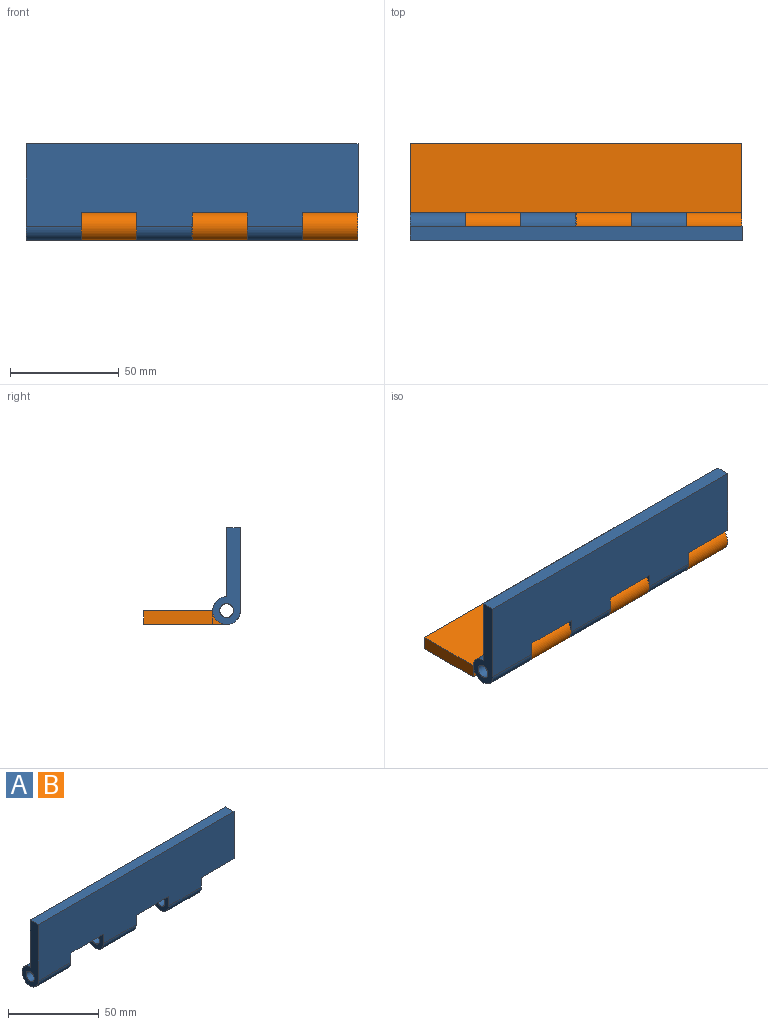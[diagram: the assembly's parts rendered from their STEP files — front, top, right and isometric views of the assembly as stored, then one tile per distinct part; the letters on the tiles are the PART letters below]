
ASSEMBLY  parts=2 mates=1
PART A: 19 faces, bbox 152.4x12.7x44.5 mm
  f0: cylinder r=6.35mm len=25.4mm, axis (-1,0,0), area 760.1mm2, adj f3,f4,f14,f18
  f1: cylinder r=6.35mm len=25.4mm, axis (-1,0,0), area 760.1mm2, adj f3,f4,f10,f15
  f2: cylinder r=6.35mm len=25.4mm, axis (-1,0,0), area 760.1mm2, adj f3,f4,f7,f11
  f3: plane 152.4x38.1mm, normal (0,-1,0), area 5322.6mm2, adj f0,f1,f2,f5,f6,f7,f9,f10
  f4: plane 152.4x31.75mm, normal (0,1,0), area 4838.7mm2, adj f0,f1,f2,f5,f6,f7,f9,f13
  f5: plane 152.4x6.35mm, normal (0,0,1), area 967.7mm2, adj f3,f4,f6,f7
  f6: plane 31.75x6.35mm, normal (1,0,0), area 201.6mm2, adj f3,f4,f5,f17
  f7: plane 44.45x12.7mm, normal (-1,0,0), area 305.3mm2, adj f2,f3,f4,f5,f8
  f8: cylinder r=3.17mm len=25.4mm, axis (1,0,0), area 506.7mm2, adj f7,f11
  f9: plane 25.4x6.35mm, normal (0,0,-1), area 161.3mm2, adj f3,f4,f10,f11
  f10: plane 12.7x12.7mm, normal (-1,0,0), area 103.7mm2, adj f1,f3,f9,f12
  f11: plane 12.7x12.7mm, normal (1,0,0), area 103.7mm2, adj f2,f3,f8,f9
  f12: cylinder r=3.17mm len=25.4mm, axis (1,0,0), area 506.7mm2, adj f10,f15
  f13: plane 25.4x6.35mm, normal (0,0,-1), area 161.3mm2, adj f3,f4,f14,f15
  f14: plane 12.7x12.7mm, normal (-1,0,0), area 103.7mm2, adj f0,f3,f13,f16
  f15: plane 12.7x12.7mm, normal (1,0,0), area 103.7mm2, adj f1,f3,f12,f13
  f16: cylinder r=3.17mm len=25.4mm, axis (1,0,0), area 506.7mm2, adj f14,f18
  f17: plane 25.4x6.35mm, normal (0,0,-1), area 161.3mm2, adj f3,f4,f6,f18
  f18: plane 12.7x12.7mm, normal (1,0,0), area 103.7mm2, adj f0,f3,f16,f17
PART B: same geometry as A
PLACE A t=(-21.38,33.08,-13.74)mm fixed
PLACE B rot(axis=(0,0.71,0.71),180deg) t=(131.02,33.08,-13.74)mm
MATE revolute B.f0 <-> A.f0  axis (-1,0,0) through (4.02,33.08,-13.74)mm
